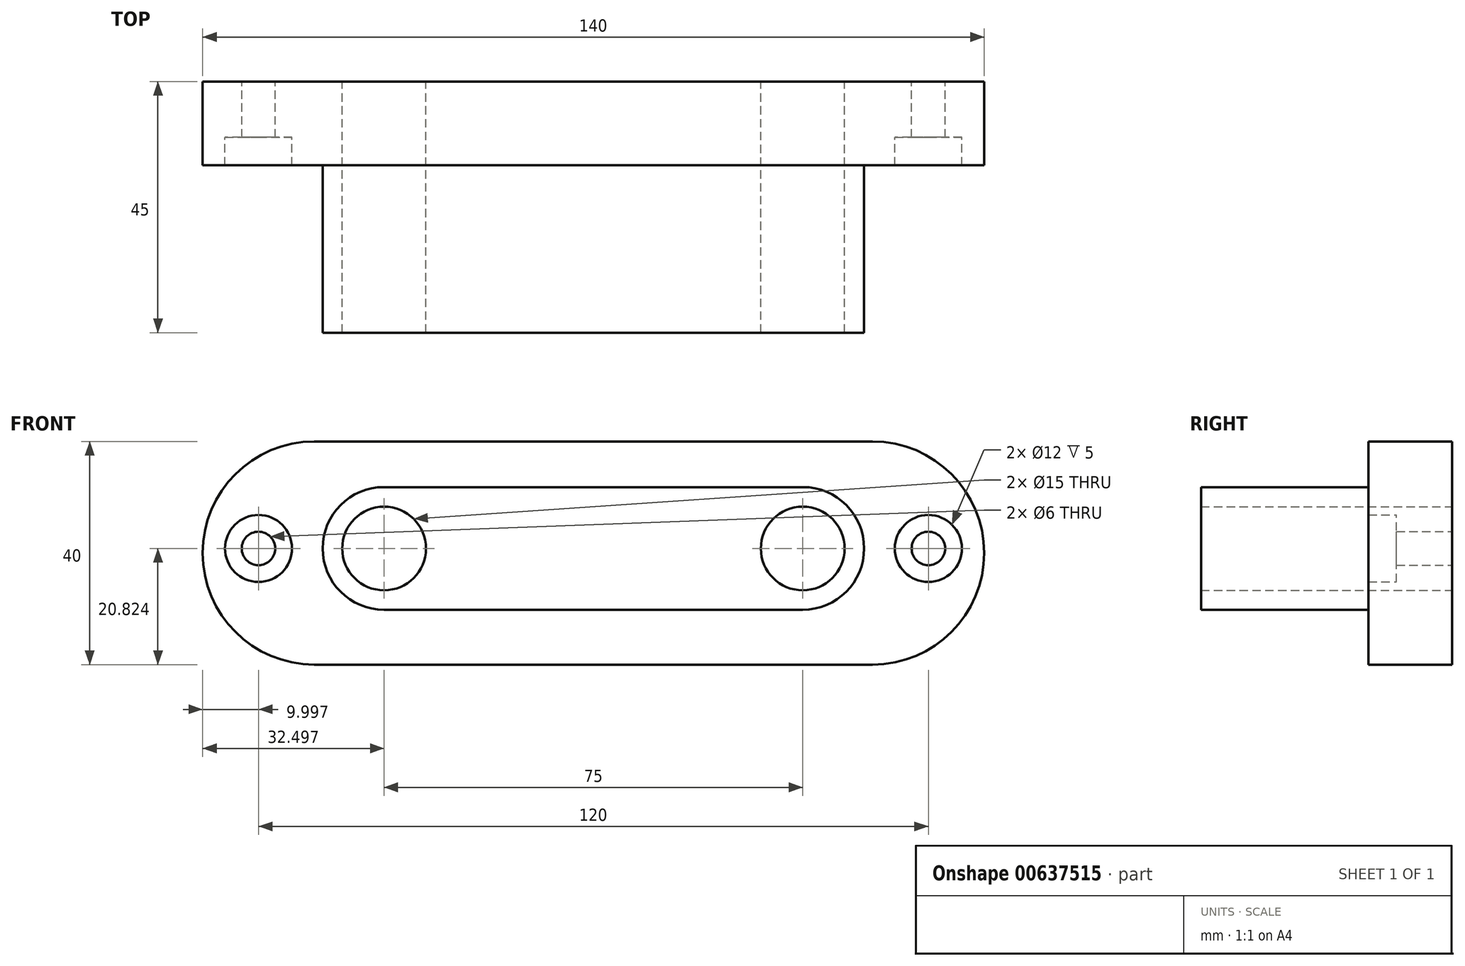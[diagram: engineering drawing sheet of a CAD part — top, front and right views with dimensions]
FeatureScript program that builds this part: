
annotation { "Feature Type Name" : "Feature", "Feature Type Description" : "" }
export const myFeature = defineFeature(function(context is Context, id is Id, definition is map)
    precondition{}
    {
        {
            var Q0;
            Q0=qCreatedBy(makeId("Front.planeOp"),FACE);
            var sketch = newSketch(context, id + "F0", { "sketchPlane" : qUnion([Q0])});
            skLineSegment(sketch, "E0.bottom", {"start": v(-40.01, 18.84) * mm, "end": v(59.99, 18.84) * mm});
            skLineSegment(sketch, "E0.top", {"start": v(-40.01, -21.16) * mm, "end": v(59.99, -21.16) * mm});
            skLineSegment(sketch, "E0.left", {"start": v(-40.01, 18.84) * mm, "end": v(-40.01, -21.16) * mm});
            skLineSegment(sketch, "E0.right", {"start": v(59.99, 18.84) * mm, "end": v(59.99, -21.16) * mm});
            skLineSegment(sketch, "E1.bottom", {"start": v(-27.51, 10.66) * mm, "end": v(47.49, 10.66) * mm});
            skLineSegment(sketch, "E1.top", {"start": v(-27.51, -11.34) * mm, "end": v(47.49, -11.34) * mm});
            skLineSegment(sketch, "E1.left", {"start": v(-27.51, 10.66) * mm, "end": v(-27.51, -11.34) * mm});
            skLineSegment(sketch, "E1.right", {"start": v(47.49, 10.66) * mm, "end": v(47.49, -11.34) * mm});
            skLineSegment(sketch, "E2", {"start": v(9.99, 10.66) * mm, "end": v(9.99, 18.84) * mm});
            skArc(sketch, "E3", {"start": v(-40.01, 18.84) * mm, "mid": v(-60.01, -1.16) * mm, "end": v(-40.01, -21.16) * mm});
            skArc(sketch, "E4", {"start": v(59.99, -21.16) * mm, "mid": v(79.99, -1.16) * mm, "end": v(59.99, 18.84) * mm});
            skArc(sketch, "E5", {"start": v(47.49, -11.34) * mm, "mid": v(58.49, -0.34) * mm, "end": v(47.49, 10.66) * mm});
            skArc(sketch, "E6", {"start": v(-27.51, 10.66) * mm, "mid": v(-38.51, -0.34) * mm, "end": v(-27.51, -11.34) * mm});
            skCircle(sketch, "E7", {"center": v(-27.51, -0.34) * mm, "radius": 7.5 * mm});
            skCircle(sketch, "E8", {"center": v(47.49, -0.34) * mm, "radius": 7.5 * mm});
            skCircle(sketch, "E9", {"center": v(-50.01, -0.34) * mm, "radius": 6 * mm});
            skCircle(sketch, "E10", {"center": v(69.99, -0.34) * mm, "radius": 6 * mm});
            skLineSegment(sketch, "E11", {"start": v(-50.01, -0.34) * mm, "end": v(69.99, -0.34) * mm});
            skCircle(sketch, "E12", {"center": v(-50.01, -0.34) * mm, "radius": 3 * mm});
            skCircle(sketch, "E13", {"center": v(69.99, -0.34) * mm, "radius": 3 * mm});
            skSolve(sketch);
        }
        {
            var Q0;
            {var subQ3=sQuery(id+"F0.wireOp",EDGE,"E2");Q0=makeQuery(id+"F0.imprint","IMPRINT",FACE,{"disambiguationData":[TD([[makeQuery(id+"F0.imprint","IMPRINT",EDGE,{"derivedFrom":subQ3}),1.0]])]});}
            var Q1;
            {var subQ0=sQuery(id+"F0.wireOp",EDGE,"E2");Q1=makeQuery(id+"F0.imprint","IMPRINT",FACE,{"disambiguationData":[TD([[makeQuery(id+"F0.imprint","IMPRINT",EDGE,{"derivedFrom":subQ0}),-1.0]])]});}
            var Q2;
            {var subQ1=sQuery(id+"F0.wireOp",EDGE,"E0.top");Q2=makeQuery(id+"F0.imprint","IMPRINT",FACE,{"disambiguationData":[TD([[makeQuery(id+"F0.imprint","IMPRINT",EDGE,{"derivedFrom":subQ1}),1.0]])]});}
            var Q3;
            {var subQ0=sQuery(id+"F0.wireOp",EDGE,"E4");Q3=makeQuery(id+"F0.imprint","IMPRINT",FACE,{"disambiguationData":[TD([[makeQuery(id+"F0.imprint","IMPRINT",EDGE,{"derivedFrom":subQ0}),1.0]])]});}
            var Q4;
            {var subQ0=sQuery(id+"F0.wireOp",EDGE,"E3");Q4=makeQuery(id+"F0.imprint","IMPRINT",FACE,{"disambiguationData":[TD([[makeQuery(id+"F0.imprint","IMPRINT",EDGE,{"derivedFrom":subQ0}),1.0]])]});}
            extrude(context, id + "F1", {"entities" : qUnion([Q0, Q1, Q2, Q3, Q4]), "depth" : 15 * mm, "offsetDistance" : 25 * mm});
        }
        {
            var Q0;
            {var subQ1=sQuery(id+"F0.wireOp",EDGE,"E1.top");Q0=makeQuery(id+"F0.imprint","IMPRINT",FACE,{"disambiguationData":[TD([[makeQuery(id+"F0.imprint","IMPRINT",EDGE,{"derivedFrom":subQ1}),1.0]])]});}
            var Q1;
            {var subQ5=sQuery(id+"F0.wireOp",EDGE,"E7");var subQ6=sQuery(id+"F0.wireOp",EDGE,"E1.left");var subQ7=makeQuery(id+"F0.imprint","INTERSECT",VERTEX,{"disambiguationData":[OD(0.0)],"derivedFrom":[subQ6,subQ5]});Q1=makeQuery(id+"F0.imprint","IMPRINT",FACE,{"disambiguationData":[TD([[makeQuery(id+"F0.imprint","IMPRINT",EDGE,{"disambiguationData":[TD([[subQ7,1.0]])],"derivedFrom":subQ5}),-1.0]])]});}
            var Q2;
            {var subQ1=sQuery(id+"F0.wireOp",EDGE,"E1.left");var subQ3=sQuery(id+"F0.wireOp",EDGE,"E7");var subQ4=makeQuery(id+"F0.imprint","INTERSECT",VERTEX,{"disambiguationData":[OD(0.0)],"derivedFrom":[subQ1,subQ3]});Q2=makeQuery(id+"F0.imprint","IMPRINT",FACE,{"disambiguationData":[TD([[makeQuery(id+"F0.imprint","IMPRINT",EDGE,{"disambiguationData":[TD([[subQ4,-1.0]])],"derivedFrom":subQ3}),-1.0]])]});}
            var Q3;
            {var subQ1=sQuery(id+"F0.wireOp",EDGE,"E1.left");var subQ3=sQuery(id+"F0.wireOp",EDGE,"E7");var subQ4=makeQuery(id+"F0.imprint","INTERSECT",VERTEX,{"disambiguationData":[OD(1.0)],"derivedFrom":[subQ1,subQ3]});Q3=makeQuery(id+"F0.imprint","IMPRINT",FACE,{"disambiguationData":[TD([[makeQuery(id+"F0.imprint","IMPRINT",EDGE,{"disambiguationData":[TD([[subQ4,1.0]])],"derivedFrom":subQ3}),-1.0]])]});}
            var Q4;
            {var subQ1=sQuery(id+"F0.wireOp",EDGE,"E1.right");var subQ3=sQuery(id+"F0.wireOp",EDGE,"E8");var subQ4=makeQuery(id+"F0.imprint","INTERSECT",VERTEX,{"disambiguationData":[OD(1.0)],"derivedFrom":[subQ1,subQ3]});Q4=makeQuery(id+"F0.imprint","IMPRINT",FACE,{"disambiguationData":[TD([[makeQuery(id+"F0.imprint","IMPRINT",EDGE,{"disambiguationData":[TD([[subQ4,-1.0]])],"derivedFrom":subQ3}),-1.0]])]});}
            var Q5;
            {var subQ1=sQuery(id+"F0.wireOp",EDGE,"E1.right");var subQ3=sQuery(id+"F0.wireOp",EDGE,"E8");var subQ4=makeQuery(id+"F0.imprint","INTERSECT",VERTEX,{"disambiguationData":[OD(0.0)],"derivedFrom":[subQ1,subQ3]});Q5=makeQuery(id+"F0.imprint","IMPRINT",FACE,{"disambiguationData":[TD([[makeQuery(id+"F0.imprint","IMPRINT",EDGE,{"disambiguationData":[TD([[subQ4,1.0]])],"derivedFrom":subQ3}),-1.0]])]});}
            extrude(context, id + "F2", {"entities" : qUnion([Q0, Q1, Q2, Q3, Q4, Q5]), "operationType" : NewBodyOperationType.ADD, "depth" : 45 * mm, "offsetDistance" : 25 * mm});
        }
        {
            var Q0;
            Q0=makeQuery(id+"F0.imprint","IMPRINT",FACE,{"disambiguationData":[TD([[makeQuery(id+"F0.imprint","IMPRINT",EDGE,{"derivedFrom":sQuery(id+"F0.wireOp",EDGE,"E10")}),1.0]])]});
            var Q1;
            Q1=makeQuery(id+"F0.imprint","IMPRINT",FACE,{"disambiguationData":[TD([[makeQuery(id+"F0.imprint","IMPRINT",EDGE,{"derivedFrom":sQuery(id+"F0.wireOp",EDGE,"E9")}),1.0]])]});
            extrude(context, id + "F3", {"entities" : qUnion([Q0, Q1]), "operationType" : NewBodyOperationType.ADD, "depth" : 10 * mm, "offsetDistance" : 25 * mm});
        }
    });
